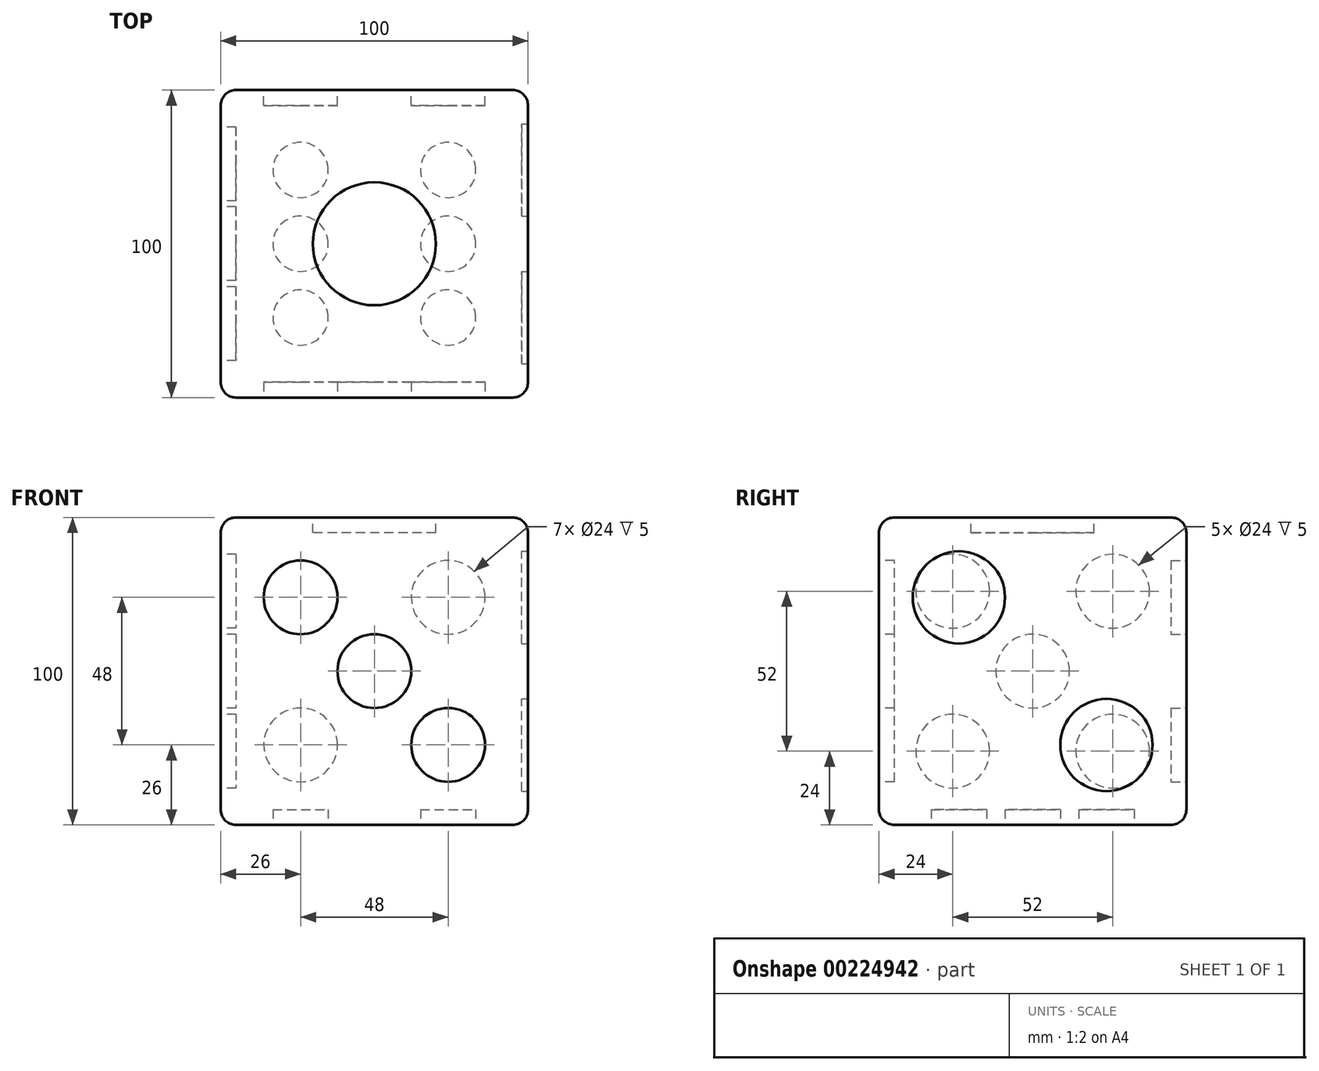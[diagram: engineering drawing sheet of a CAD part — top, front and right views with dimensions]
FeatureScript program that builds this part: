
annotation { "Feature Type Name" : "Feature", "Feature Type Description" : "" }
export const myFeature = defineFeature(function(context is Context, id is Id, definition is map)
    precondition{}
    {
        {
            var Q0;
            Q0=qCreatedBy(makeId("Front.planeOp"),FACE);
            var sketch = newSketch(context, id + "F0", { "sketchPlane" : qUnion([Q0])});
            skLineSegment(sketch, "E0.bottom", {"start": v(-50, 50) * mm, "end": v(50, 50) * mm});
            skLineSegment(sketch, "E0.top", {"start": v(-50, -50) * mm, "end": v(50, -50) * mm});
            skLineSegment(sketch, "E0.left", {"start": v(-50, 50) * mm, "end": v(-50, -50) * mm});
            skLineSegment(sketch, "E0.right", {"start": v(50, 50) * mm, "end": v(50, -50) * mm});
            skSolve(sketch);
        }
        {
            var Q0;
            Q0 = qSketchRegion(id + "F0", true);
            extrude(context, id + "F1", {"entities" : qUnion([Q0]), "endBound" : BoundingType.SYMMETRIC, "depth" : 100 * mm});
        }
        {
            var Q0;
            Q0=makeQuery(id+"F1.opExtrude","CAP_EDGE",EDGE,{"disambiguationData":[OSD([sQuery(id+"F0.wireOp",EDGE,"E0.bottom")])],"isStart":false});
            var Q1;
            Q1=makeQuery(id+"F1.opExtrude","CAP_EDGE",EDGE,{"disambiguationData":[OSD([sQuery(id+"F0.wireOp",EDGE,"E0.top")])],"isStart":true});
            var Q2;
            Q2=makeQuery(id+"F1.opExtrude","CAP_EDGE",EDGE,{"disambiguationData":[OSD([sQuery(id+"F0.wireOp",EDGE,"E0.top")])],"isStart":false});
            var Q3;
            Q3=makeQuery(id+"F1.opExtrude","CAP_EDGE",EDGE,{"disambiguationData":[OSD([sQuery(id+"F0.wireOp",EDGE,"E0.bottom")])],"isStart":true});
            fillet(context, id + "F2", {"entities" : qUnion([Q0, Q1, Q2, Q3]), "radius" : 5 * mm, "tangentPropagation" : true, "allowEdgeOverflow" : false});
        }
        {
            var Q0;
            Q0=makeQuery(id+"F1.opExtrude","SWEPT_EDGE",EDGE,{"disambiguationData":[OSD([sQuery(id+"F0.wireOp",EDGE,"E0.bottom"),sQuery(id+"F0.wireOp",EDGE,"E0.right")])]});
            var Q1;
            Q1=makeQuery(id+"F1.opExtrude","SWEPT_EDGE",EDGE,{"disambiguationData":[OSD([sQuery(id+"F0.wireOp",EDGE,"E0.bottom"),sQuery(id+"F0.wireOp",EDGE,"E0.left")])]});
            fillet(context, id + "F3", {"entities" : qUnion([Q0, Q1]), "radius" : 5 * mm, "tangentPropagation" : true, "allowEdgeOverflow" : false});
        }
        {
            var Q0;
            Q0=makeQuery(id+"F1.opExtrude","SWEPT_FACE",FACE,{"disambiguationData":[OSD([sQuery(id+"F0.wireOp",EDGE,"E0.bottom")])]});
            var sketch = newSketch(context, id + "F4", { "sketchPlane" : qUnion([Q0])});
            skCircle(sketch, "E1", {"center": v(0, 0) * mm, "radius": 20 * mm});
            skSolve(sketch);
        }
        {
            var Q0;
            Q0=makeQuery(id+"F4.imprint","IMPRINT",FACE,{"disambiguationData":[TD([[makeQuery(id+"F4.imprint","IMPRINT",EDGE,{"derivedFrom":sQuery(id+"F4.wireOp",EDGE,"E1")}),1.0]])]});
            extrude(context, id + "F5", {"entities" : qUnion([Q0]), "operationType" : NewBodyOperationType.REMOVE, "oppositeDirection" : true, "depth" : 5 * mm});
        }
        {
            var Q0;
            Q0=makeQuery(id+"F1.opExtrude","SWEPT_FACE",FACE,{"disambiguationData":[OSD([sQuery(id+"F0.wireOp",EDGE,"E0.top")])]});
            var sketch = newSketch(context, id + "F6", { "sketchPlane" : qUnion([Q0])});
            skCircle(sketch, "E2", {"center": v(-24, -24) * mm, "radius": 9 * mm});
            skCircle(sketch, "E3", {"center": v(-24, 24) * mm, "radius": 9 * mm});
            skCircle(sketch, "E4", {"center": v(-24, 0) * mm, "radius": 9 * mm});
            skCircle(sketch, "E5.MirrorC", {"center": v(24, 24) * mm, "radius": 9 * mm});
            skCircle(sketch, "E6.MirrorC", {"center": v(24, 0) * mm, "radius": 9 * mm});
            skCircle(sketch, "E7.MirrorC", {"center": v(24, -24) * mm, "radius": 9 * mm});
            skSolve(sketch);
        }
        {
            var Q0;
            Q0 = qSketchRegion(id + "F6", true);
            extrude(context, id + "F7", {"entities" : qUnion([Q0]), "operationType" : NewBodyOperationType.REMOVE, "oppositeDirection" : true, "depth" : 5 * mm});
        }
        {
            var Q0;
            Q0=makeQuery(id+"F1.opExtrude","CAP_FACE",FACE,{"disambiguationData":[OSD([sQuery(id+"F0.wireOp",EDGE,"E0.bottom"),sQuery(id+"F0.wireOp",EDGE,"E0.top"),sQuery(id+"F0.wireOp",EDGE,"E0.left"),sQuery(id+"F0.wireOp",EDGE,"E0.right")])],"isStart":false});
            var sketch = newSketch(context, id + "F8", { "sketchPlane" : qUnion([Q0])});
            skCircle(sketch, "E8", {"center": v(-24, 24) * mm, "radius": 12 * mm});
            skCircle(sketch, "E9", {"center": v(0, 0) * mm, "radius": 12 * mm});
            skCircle(sketch, "E10", {"center": v(24, -24) * mm, "radius": 12 * mm});
            skSolve(sketch);
        }
        {
            var Q0;
            Q0 = qSketchRegion(id + "F8", true);
            extrude(context, id + "F9", {"entities" : qUnion([Q0]), "operationType" : NewBodyOperationType.REMOVE, "oppositeDirection" : true, "depth" : 5 * mm});
        }
        {
            var Q0;
            Q0=makeQuery(id+"F1.opExtrude","CAP_FACE",FACE,{"disambiguationData":[OSD([sQuery(id+"F0.wireOp",EDGE,"E0.bottom"),sQuery(id+"F0.wireOp",EDGE,"E0.top"),sQuery(id+"F0.wireOp",EDGE,"E0.left"),sQuery(id+"F0.wireOp",EDGE,"E0.right")])],"isStart":true});
            var sketch = newSketch(context, id + "F10", { "sketchPlane" : qUnion([Q0])});
            skCircle(sketch, "E11", {"center": v(24, 24) * mm, "radius": 12 * mm});
            skCircle(sketch, "E12", {"center": v(-24, 24) * mm, "radius": 12 * mm});
            skCircle(sketch, "E13.MirrorC", {"center": v(24, -24) * mm, "radius": 12 * mm});
            skCircle(sketch, "E14.MirrorC", {"center": v(-24, -24) * mm, "radius": 12 * mm});
            skSolve(sketch);
        }
        {
            var Q0;
            Q0 = qSketchRegion(id + "F10", true);
            extrude(context, id + "F11", {"entities" : qUnion([Q0]), "operationType" : NewBodyOperationType.REMOVE, "oppositeDirection" : true, "depth" : 5 * mm});
        }
        {
            var Q0;
            Q0=makeQuery(id+"F1.opExtrude","SWEPT_FACE",FACE,{"disambiguationData":[OSD([sQuery(id+"F0.wireOp",EDGE,"E0.right")])]});
            var sketch = newSketch(context, id + "F12", { "sketchPlane" : qUnion([Q0])});
            skCircle(sketch, "E15", {"center": v(-24, 24) * mm, "radius": 15 * mm});
            skCircle(sketch, "E16", {"center": v(24, -24) * mm, "radius": 15 * mm});
            skSolve(sketch);
        }
        {
            var Q0;
            Q0 = qSketchRegion(id + "F12", true);
            extrude(context, id + "F13", {"entities" : qUnion([Q0]), "operationType" : NewBodyOperationType.REMOVE, "oppositeDirection" : true, "depth" : 2 * mm});
        }
        {
            var Q0;
            Q0=makeQuery(id+"F1.opExtrude","SWEPT_FACE",FACE,{"disambiguationData":[OSD([sQuery(id+"F0.wireOp",EDGE,"E0.left")])]});
            var sketch = newSketch(context, id + "F14", { "sketchPlane" : qUnion([Q0])});
            skCircle(sketch, "E17", {"center": v(-26, 26) * mm, "radius": 12 * mm});
            skCircle(sketch, "E18", {"center": v(26, 26) * mm, "radius": 12 * mm});
            skCircle(sketch, "E19", {"center": v(0, 0) * mm, "radius": 12 * mm});
            skCircle(sketch, "E20.MirrorC", {"center": v(-26, -26) * mm, "radius": 12 * mm});
            skCircle(sketch, "E21.MirrorC", {"center": v(26, -26) * mm, "radius": 12 * mm});
            skSolve(sketch);
        }
        {
            var Q0;
            Q0 = qSketchRegion(id + "F14", true);
            extrude(context, id + "F15", {"entities" : qUnion([Q0]), "operationType" : NewBodyOperationType.REMOVE, "oppositeDirection" : true, "depth" : 5 * mm});
        }
    });
